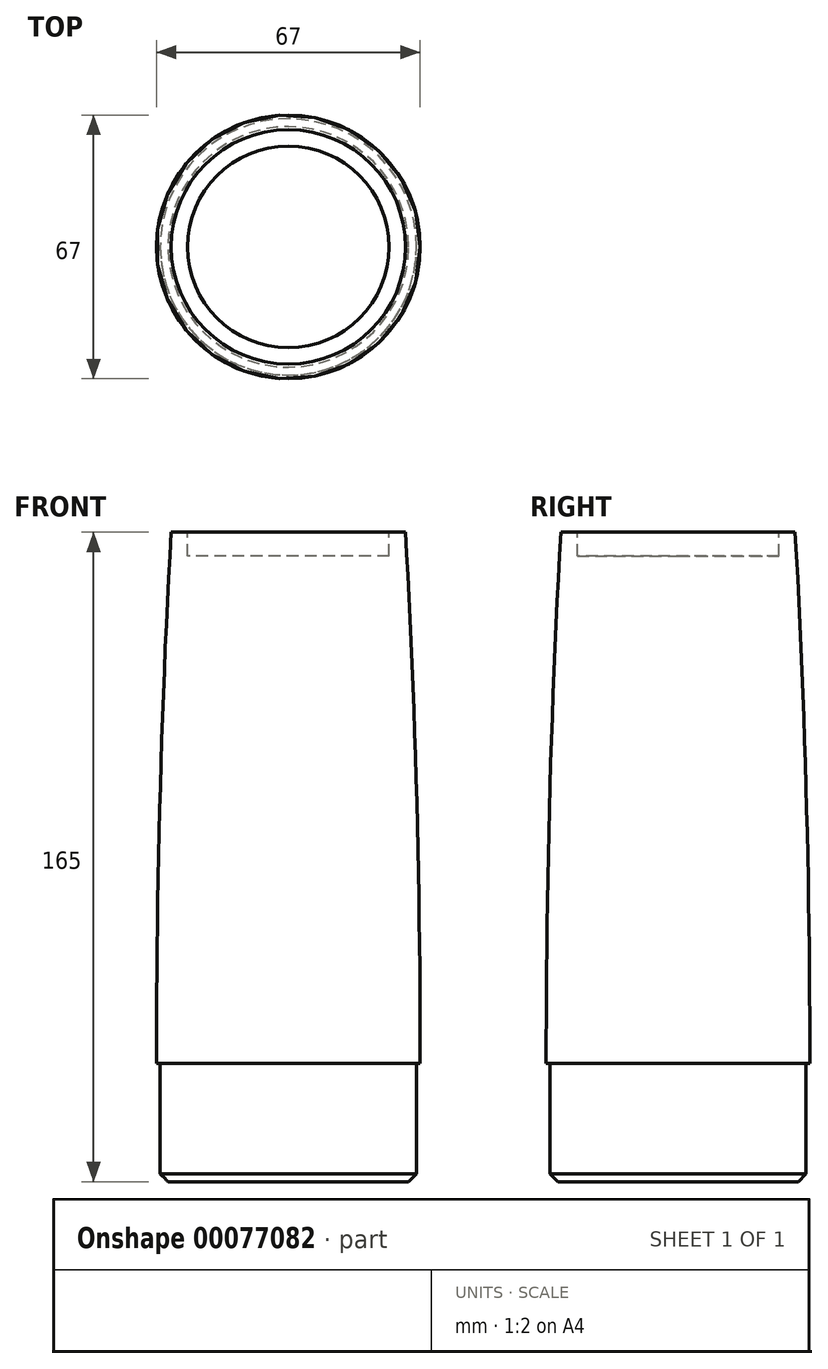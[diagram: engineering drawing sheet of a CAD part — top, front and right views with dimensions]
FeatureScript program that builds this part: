
annotation { "Feature Type Name" : "Feature", "Feature Type Description" : "" }
export const myFeature = defineFeature(function(context is Context, id is Id, definition is map)
    precondition{}
    {
        {
            var Q0;
            Q0=qCreatedBy(makeId("Front.planeOp"),FACE);
            var sketch = newSketch(context, id + "F0", { "sketchPlane" : qUnion([Q0])});
            skEllipticalArc(sketch, "E0", {});
            skLineSegment(sketch, "E1", {"start": v(0, 129) * mm, "end": v(0, -294) * mm, "construction": true});
            skPoint(sketch, "E1.endSnap0", {"position": v(0, 294) * mm});
            skLineSegment(sketch, "E2", {"start": v(-33.5, 0) * mm, "end": v(-32.55, 0) * mm, "construction": true});
            skPoint(sketch, "E2.endSnap0", {"position": v(33.5, 0) * mm});
            skPoint(sketch, "E3.orphan", {"position": v(0, 67.2) * mm});
            skPoint(sketch, "E4.orphan", {"position": v(0, -68.03) * mm});
            skLineSegment(sketch, "E5", {"start": v(-33.5, 0) * mm, "end": v(-32.55, 0) * mm});
            skLineSegment(sketch, "E6", {"start": v(-32.55, 0) * mm, "end": v(-32.55, -30) * mm});
            skLineSegment(sketch, "E7", {"start": v(-32.55, -30) * mm, "end": v(0, -30) * mm});
            skLineSegment(sketch, "E8", {"start": v(0, -30) * mm, "end": v(0, 294) * mm});
            skLineSegment(sketch, "E9.bottom", {"start": v(-32.55, 0) * mm, "end": v(-33.5, 0) * mm});
            skLineSegment(sketch, "E9.top", {"start": v(-25.6, 135) * mm, "end": v(-29.76, 135) * mm});
            skLineSegment(sketch, "E9.left", {"start": v(0, 0) * mm, "end": v(0, 129) * mm});
            skPoint(sketch, "E9.right.end.orphan", {"position": v(-47.64, 135) * mm});
            skPoint(sketch, "E10.orphan", {"position": v(-47.64, 0) * mm});
            skLineSegment(sketch, "E11.trimOffspring", {"start": v(0, 0) * mm, "end": v(40.39, 0) * mm, "construction": true});
            skPoint(sketch, "E12.orphan", {"position": v(-35.36, 0) * mm});
            skLineSegment(sketch, "E13.top", {"start": v(0, 129) * mm, "end": v(-25.6, 129) * mm});
            skLineSegment(sketch, "E13.right", {"start": v(-25.6, 135) * mm, "end": v(-25.6, 129) * mm});
            skPoint(sketch, "E14.orphan", {"position": v(0, 135) * mm});
            const initialGuessF0  = {"E0": [0, 0, 0, 1, 0.294, 0.0335, 1.0937202801470427, 1.5707963267948966]};
            skSetInitialGuess(sketch, initialGuessF0);
            skSolve(sketch);
        }
        {
            var Q0;
            Q0=makeQuery(id+"F0.imprint","IMPRINT",FACE,{"disambiguationData":[TD([[makeQuery(id+"F0.imprint","IMPRINT",EDGE,{"derivedFrom":sQuery(id+"F0.wireOp",EDGE,"E0")}),1.0]])]});
            var Q1;
            Q1=sQuery(id+"F0.wireOp",EDGE,"E1");
            revolve(context, id + "F1", {"entities" : qUnion([Q0]), "axis" : qUnion([Q1]), "revolveType" : RevolveType.FULL});
        }
        {
            var Q0;
            Q0=makeQuery(id+"F1.opRevolve","SWEPT_EDGE",EDGE,{"disambiguationData":[OSD([sQuery(id+"F0.wireOp",EDGE,"E6"),sQuery(id+"F0.wireOp",EDGE,"E7")])]});
            chamfer(context, id + "F2", {"entities" : qUnion([Q0]), "width" : 2 * mm, "tangentPropagation" : true});
        }
    });
